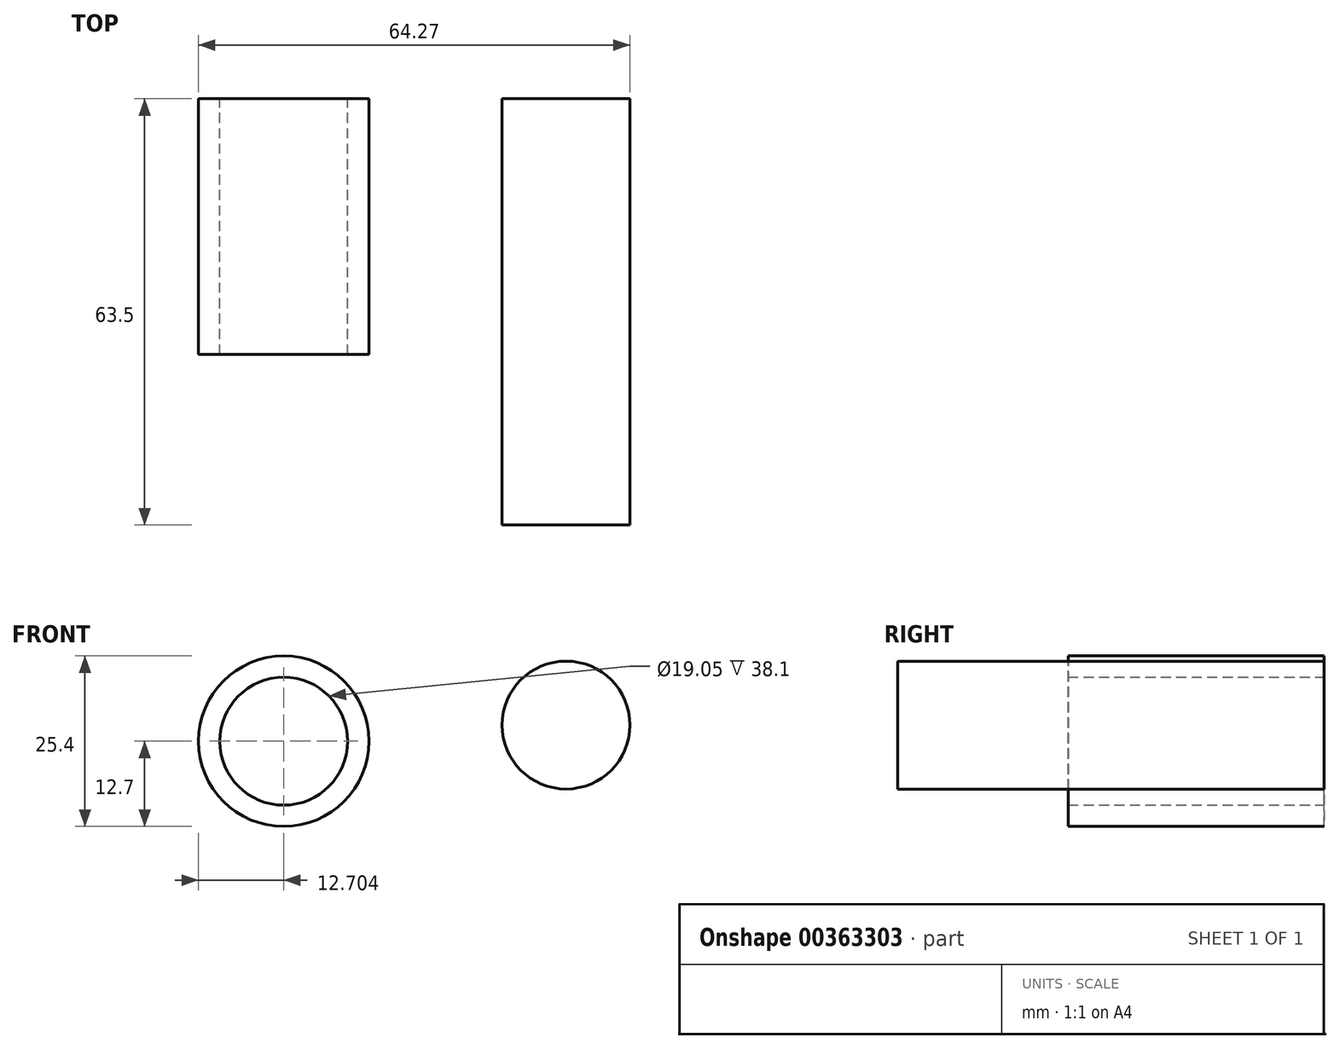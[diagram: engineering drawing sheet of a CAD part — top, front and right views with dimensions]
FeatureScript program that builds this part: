
annotation { "Feature Type Name" : "Feature", "Feature Type Description" : "" }
export const myFeature = defineFeature(function(context is Context, id is Id, definition is map)
    precondition{}
    {
        {
            var Q0;
            Q0=qCreatedBy(makeId("Front.planeOp"),FACE);
            var sketch = newSketch(context, id + "F0", { "sketchPlane" : qUnion([Q0])});
            skCircle(sketch, "E0", {"center": v(-63.42, 41.38) * mm, "radius": 12.7 * mm});
            skCircle(sketch, "E1", {"center": v(-21.37, 43.78) * mm, "radius": 9.53 * mm});
            skCircle(sketch, "E2", {"center": v(-63.42, 41.38) * mm, "radius": 9.53 * mm});
            skSolve(sketch);
        }
        {
            var Q0;
            Q0 = qSketchRegion(id + "F0", true);
            extrude(context, id + "F1", {"entities" : qUnion([Q0]), "depth" : 38.1 * mm});
        }
        {
            var Q0;
            Q0=makeQuery(id+"F1.opExtrude","CAP_FACE",FACE,{"disambiguationData":[OSD([sQuery(id+"F0.wireOp",EDGE,"E1")])],"isStart":false});
            extrude(context, id + "F2", {"entities" : qUnion([Q0]), "operationType" : NewBodyOperationType.ADD, "depth" : 25.4 * mm});
        }
    });
